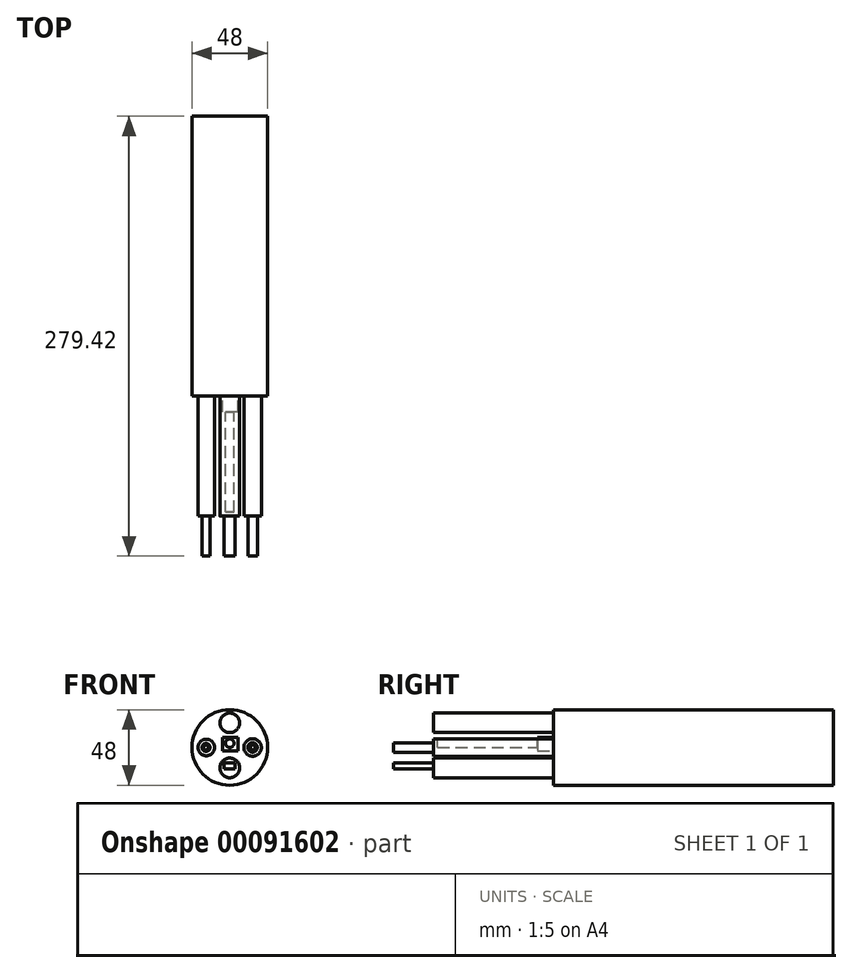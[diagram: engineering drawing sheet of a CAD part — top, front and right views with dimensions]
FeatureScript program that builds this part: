
annotation { "Feature Type Name" : "Feature", "Feature Type Description" : "" }
export const myFeature = defineFeature(function(context is Context, id is Id, definition is map)
    precondition{}
    {
        {
            var Q0;
            Q0=qCreatedBy(makeId("Front.planeOp"),FACE);
            var sketch = newSketch(context, id + "F0", { "sketchPlane" : qUnion([Q0])});
            skCircle(sketch, "E0", {"center": v(0, 0) * mm, "radius": 24 * mm});
            skSolve(sketch);
        }
        {
            var Q0;
            Q0 = qSketchRegion(id + "F0", true);
            extrude(context, id + "F1", {"entities" : qUnion([Q0]), "depth" : 177.8 * mm});
        }
        {
            var Q0;
            Q0=makeQuery(id+"F1.opExtrude","CAP_FACE",FACE,{"disambiguationData":[OSD([sQuery(id+"F0.wireOp",EDGE,"E0")])],"isStart":false});
            var sketch = newSketch(context, id + "F2", { "sketchPlane" : qUnion([Q0])});
            skCircle(sketch, "E1", {"center": v(-14.88, 0) * mm, "radius": 5.26 * mm});
            skCircle(sketch, "E2", {"center": v(14.5, 0) * mm, "radius": 5.56 * mm});
            skSolve(sketch);
        }
        {
            var Q0;
            Q0 = qSketchRegion(id + "F2", true);
            extrude(context, id + "F3", {"entities" : qUnion([Q0]), "operationType" : NewBodyOperationType.ADD, "depth" : 76.2 * mm});
        }
        {
            var Q0;
            Q0=makeQuery(id+"F3.opExtrude","CAP_FACE",FACE,{"disambiguationData":[OSD([sQuery(id+"F2.wireOp",EDGE,"E2")])],"isStart":false});
            var sketch = newSketch(context, id + "F4", { "sketchPlane" : qUnion([Q0])});
            skCircle(sketch, "E3", {"center": v(-15.07, 0) * mm, "radius": 2.54 * mm});
            skCircle(sketch, "E4", {"center": v(14.5, 0) * mm, "radius": 3.03 * mm});
            skSolve(sketch);
        }
        {
            var Q0;
            Q0 = qSketchRegion(id + "F4", true);
            extrude(context, id + "F5", {"entities" : qUnion([Q0]), "operationType" : NewBodyOperationType.ADD, "depth" : 25.4 * mm});
        }
        {
            var Q0;
            Q0=makeQuery(id+"F5.opExtrude","CAP_FACE",FACE,{"disambiguationData":[OSD([sQuery(id+"F4.wireOp",EDGE,"E3")])],"isStart":false});
            var sketch = newSketch(context, id + "F6", { "sketchPlane" : qUnion([Q0])});
            skCircle(sketch, "E5", {"center": v(-15.07, 0) * mm, "radius": 1.48 * mm});
            skCircle(sketch, "E6", {"center": v(14.53, 0) * mm, "radius": 1.49 * mm});
            skSolve(sketch);
        }
        {
            var Q0;
            Q0 = qSketchRegion(id + "F6", true);
            extrude(context, id + "F7", {"entities" : qUnion([Q0]), "operationType" : NewBodyOperationType.ADD, "depth" : 1 / 50.8 * mm});
        }
        {
            var Q0;
            Q0=makeQuery(id+"F1.opExtrude","CAP_FACE",FACE,{"disambiguationData":[OSD([sQuery(id+"F0.wireOp",EDGE,"E0")])],"isStart":false});
            var sketch = newSketch(context, id + "F8", { "sketchPlane" : qUnion([Q0])});
            skLineSegment(sketch, "E7.bottom", {"start": v(5.29, 6.43) * mm, "end": v(-4.7, 6.43) * mm});
            skLineSegment(sketch, "E7.top", {"start": v(5.29, -2.34) * mm, "end": v(-4.7, -2.34) * mm});
            skLineSegment(sketch, "E7.left", {"start": v(5.29, 6.43) * mm, "end": v(5.29, -2.34) * mm});
            skLineSegment(sketch, "E7.right", {"start": v(-4.7, 6.43) * mm, "end": v(-4.7, -2.34) * mm});
            skSolve(sketch);
        }
        {
            var Q0;
            Q0 = qSketchRegion(id + "F8", true);
            extrude(context, id + "F9", {"entities" : qUnion([Q0]), "operationType" : NewBodyOperationType.ADD, "depth" : 10.16 * mm});
        }
        {
            var Q0;
            Q0=makeQuery(id+"F9.opExtrude","CAP_FACE",FACE,{"disambiguationData":[OSD([sQuery(id+"F8.wireOp",EDGE,"E7.bottom"),sQuery(id+"F8.wireOp",EDGE,"E7.top"),sQuery(id+"F8.wireOp",EDGE,"E7.left"),sQuery(id+"F8.wireOp",EDGE,"E7.right")])],"isStart":false});
            var sketch = newSketch(context, id + "F10", { "sketchPlane" : qUnion([Q0])});
            skCircle(sketch, "E8", {"center": v(0, 2.68) * mm, "radius": 2.68 * mm});
            skSolve(sketch);
        }
        {
            var Q0;
            Q0 = qSketchRegion(id + "F10", true);
            extrude(context, id + "F11", {"entities" : qUnion([Q0]), "operationType" : NewBodyOperationType.ADD, "depth" : 63.5 * mm});
        }
        {
            var Q0;
            Q0=makeQuery(id+"F1.opExtrude","CAP_FACE",FACE,{"disambiguationData":[OSD([sQuery(id+"F0.wireOp",EDGE,"E0")])],"isStart":false});
            var sketch = newSketch(context, id + "F12", { "sketchPlane" : qUnion([Q0])});
            skCircle(sketch, "E9", {"center": v(0, -12.96) * mm, "radius": 6.26 * mm});
            skSolve(sketch);
        }
        {
            var Q0;
            Q0 = qSketchRegion(id + "F12", true);
            extrude(context, id + "F13", {"entities" : qUnion([Q0]), "operationType" : NewBodyOperationType.ADD, "depth" : 76.2 * mm});
        }
        {
            var Q0;
            Q0=makeQuery(id+"F13.opExtrude","CAP_FACE",FACE,{"disambiguationData":[OSD([sQuery(id+"F12.wireOp",EDGE,"E9")])],"isStart":false});
            var sketch = newSketch(context, id + "F14", { "sketchPlane" : qUnion([Q0])});
            skLineSegment(sketch, "E10.bottom", {"start": v(3.38, -13.52) * mm, "end": v(-3.52, -13.52) * mm});
            skLineSegment(sketch, "E10.top", {"start": v(3.38, -9.86) * mm, "end": v(-3.52, -9.86) * mm});
            skLineSegment(sketch, "E10.left", {"start": v(3.38, -13.52) * mm, "end": v(3.38, -9.86) * mm});
            skLineSegment(sketch, "E10.right", {"start": v(-3.52, -13.52) * mm, "end": v(-3.52, -9.86) * mm});
            skSolve(sketch);
        }
        {
            var Q0;
            Q0 = qSketchRegion(id + "F14", true);
            extrude(context, id + "F15", {"entities" : qUnion([Q0]), "operationType" : NewBodyOperationType.ADD, "depth" : 25.4 * mm});
        }
        {
            var Q0;
            Q0=makeQuery(id+"F1.opExtrude","CAP_FACE",FACE,{"disambiguationData":[OSD([sQuery(id+"F0.wireOp",EDGE,"E0")])],"isStart":false});
            var sketch = newSketch(context, id + "F16", { "sketchPlane" : qUnion([Q0])});
            skCircle(sketch, "E11", {"center": v(0, 15.63) * mm, "radius": 6.2 * mm});
            skSolve(sketch);
        }
        {
            var Q0;
            Q0 = qSketchRegion(id + "F16", true);
            extrude(context, id + "F17", {"entities" : qUnion([Q0]), "operationType" : NewBodyOperationType.ADD, "depth" : 76.2 * mm});
        }
    });
